# Revit family: Vuelift_Octagonal_Glass_2-Story
name_source: partatom
category: Generic Models
units: mm (PartAtom-declared; Revit-internal decimal feet)

## family parameters
Always vertical = Yes
Can host rebar = No
Classification Number = 23.50.05.14
Cut with Voids When Loaded = No
Maintain Annotation Orientation = No
Part Type = Normal
Room Calculation Point = No
Round Connector Dimension = Use Diameter
Shared = No
Work Plane-Based = No

## types (3) — shared parameters
76.5" H Cab = 76 1/2"
84" H Cab = 84"
Applied Code = ASME 17.1-2016 SEC. 5.3
Cabinet Floor Area = 44x42",12ft2, 1.1x1.0m, 1.2m2
Cabinet Interior Height = 84'' [2.13 m]
Cabinet Weight = 1050 lb (476 kg)
Capacity = 950 lbs (432 kg)
Classification = Residential Building
Default Elevation = 0"
Elevator Height = 84"
Glass = Glass
Height From Top Floor to Elevator Top XX = 96"
Hoistway Door = 84"
Load = 0 VA
Manufacturer = Savaria
Model = Octagonal Glass
Number of Floors = 2 Max.
Poles = 1
Power Supply = 60 Hz Single Phase 240 volt (60Hz)
Specification = https://276ajivls9v24coqa255x2fb-wpengine.netdna-ssl.com
URL = https://www.savaria.com
Voltage_x = 0 V
Walls = Glass Cab

## per-type parameters (varying)
| type | 76.5" Cabin Visibility | 84" Cabin Visibility | Frame | Height From Top Floor to Elevator Top | Height From Top Floor to Elevator Top_Reverse |
| Octagonal Glass - Black Sandtex | Yes | No | Powder Coat - Savaria - Black Sandtex | 96" | 106" |
| Octagonal Glass - White Sandtex | No | Yes | Powder Coat - Savaria - White Sandtex | 106" | 96" |
| Octagonal Glass - Silver Sandtex | No | Yes | Powder Coat - Savaria - Silver Sandtex | 106" | 96" |

## geometry (parser evidence)
native form markers: Sweep x23
no freeform markers — native parametric forms only
